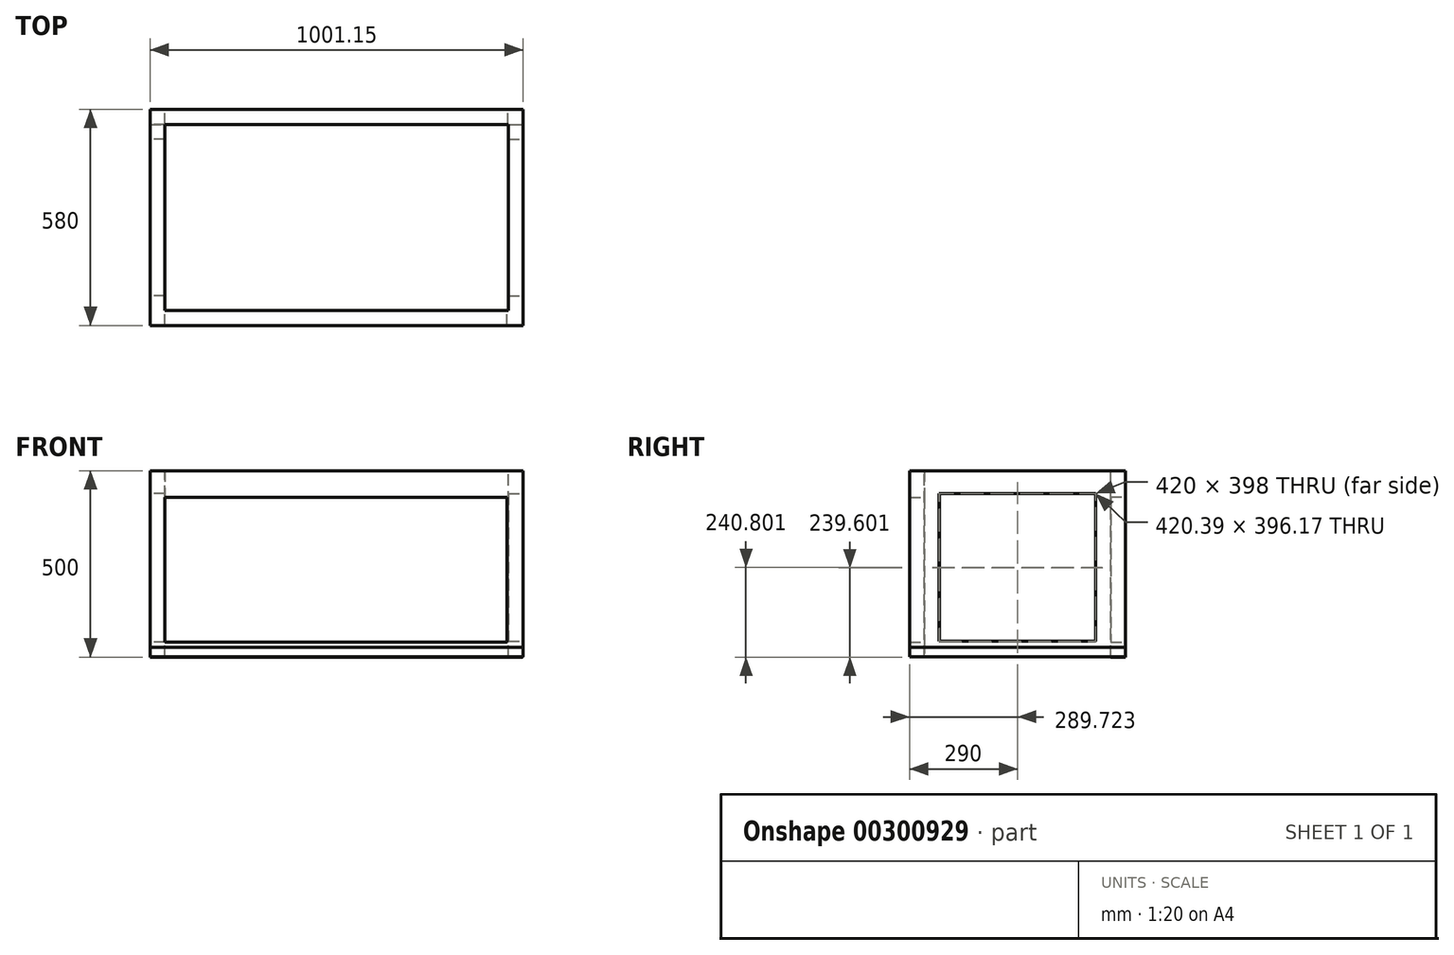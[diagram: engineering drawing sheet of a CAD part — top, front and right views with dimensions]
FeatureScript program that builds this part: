
annotation { "Feature Type Name" : "Feature", "Feature Type Description" : "" }
export const myFeature = defineFeature(function(context is Context, id is Id, definition is map)
    precondition{}
    {
        {
            var Q0;
            Q0=qCreatedBy(makeId("Front.planeOp"),FACE);
            var sketch = newSketch(context, id + "F0", { "sketchPlane" : qUnion([Q0])});
            skLineSegment(sketch, "E0.bottom", {"start": v(-500, -291.67) * mm, "end": v(500, -291.67) * mm});
            skLineSegment(sketch, "E0.top", {"start": v(-500, 208.33) * mm, "end": v(500, 208.33) * mm});
            skLineSegment(sketch, "E0.left", {"start": v(-500, -291.67) * mm, "end": v(-500, 208.33) * mm});
            skLineSegment(sketch, "E0.right", {"start": v(500, -291.67) * mm, "end": v(500, 208.33) * mm});
            skPoint(sketch, "E0.middle", {"position": v(0, -41.67) * mm});
            skLineSegment(sketch, "E1.bottom", {"start": v(-460, 138.33) * mm, "end": v(460, 138.33) * mm});
            skLineSegment(sketch, "E1.top", {"start": v(-460, -251.67) * mm, "end": v(460, -251.67) * mm});
            skLineSegment(sketch, "E1.left", {"start": v(-460, 138.33) * mm, "end": v(-460, -251.67) * mm});
            skLineSegment(sketch, "E1.right", {"start": v(460, 138.33) * mm, "end": v(460, -251.67) * mm});
            skLineSegment(sketch, "E2", {"start": v(-460, 138.33) * mm, "end": v(-500, 138.33) * mm});
            skLineSegment(sketch, "E3", {"start": v(460, 138.33) * mm, "end": v(500, 138.33) * mm});
            skSolve(sketch);
        }
        {
            var Q0;
            Q0 = qSketchRegion(id + "FjWjyGHS0iHYbx7_1", true);
            var Q1;
            {var subQ1=sQuery(id+"F0.wireOp",EDGE,"E0.top");Q1=makeQuery(id+"F0.imprint","IMPRINT",FACE,{"disambiguationData":[TD([[makeQuery(id+"F0.imprint","IMPRINT",EDGE,{"derivedFrom":subQ1}),-1.0]])]});}
            var Q2;
            {var subQ1=sQuery(id+"F0.wireOp",EDGE,"E0.bottom");Q2=makeQuery(id+"F0.imprint","IMPRINT",FACE,{"disambiguationData":[TD([[makeQuery(id+"F0.imprint","IMPRINT",EDGE,{"derivedFrom":subQ1}),1.0]])]});}
            extrude(context, id + "F1", {"entities" : qUnion([Q0, Q1, Q2]), "depth" : 40 * mm});
        }
        {
            var Q0;
            {var subQ1=sQuery(id+"F0.wireOp",EDGE,"E0.bottom");Q0=makeQuery(id+"F0.imprint","IMPRINT",FACE,{"disambiguationData":[TD([[makeQuery(id+"F0.imprint","IMPRINT",EDGE,{"derivedFrom":subQ1}),1.0]])]});}
            var Q1;
            {var subQ1=sQuery(id+"F0.wireOp",EDGE,"E0.top");Q1=makeQuery(id+"F0.imprint","IMPRINT",FACE,{"disambiguationData":[TD([[makeQuery(id+"F0.imprint","IMPRINT",EDGE,{"derivedFrom":subQ1}),-1.0]])]});}
            extrude(context, id + "F2", {"entities" : qUnion([Q0, Q1]), "depth" : 40 * mm});
        }
        {
            var Q0;
            Q0=makeQuery(id+"F2.opExtrude","SWEPT_FACE",FACE,{"disambiguationData":[OSD([sQuery(id+"F0.wireOp",EDGE,"E0.left")])]});
            var sketch = newSketch(context, id + "F3", { "sketchPlane" : qUnion([Q0])});
            skLineSegment(sketch, "E4.bottom", {"start": v(40, 146.93) * mm, "end": v(540, 146.93) * mm});
            skLineSegment(sketch, "E4.top", {"start": v(40, -291.07) * mm, "end": v(540, -291.07) * mm});
            skLineSegment(sketch, "E4.left", {"start": v(40, 146.93) * mm, "end": v(40, -291.07) * mm});
            skLineSegment(sketch, "E4.right", {"start": v(540, 146.93) * mm, "end": v(540, -291.07) * mm});
            skLineSegment(sketch, "E5.bottom", {"start": v(40, 208.33) * mm, "end": v(540, 208.33) * mm});
            skLineSegment(sketch, "E5.left", {"start": v(40, 208.33) * mm, "end": v(40, 146.93) * mm});
            skLineSegment(sketch, "E5.right", {"start": v(540, 208.33) * mm, "end": v(540, 146.93) * mm});
            skLineSegment(sketch, "E6.top", {"start": v(80, -251.07) * mm, "end": v(500, -251.07) * mm});
            skLineSegment(sketch, "E6.left", {"start": v(80, 146.93) * mm, "end": v(80, -251.07) * mm});
            skLineSegment(sketch, "E6.right", {"start": v(500, 146.93) * mm, "end": v(500, -251.07) * mm});
            skSolve(sketch);
        }
        {
            var Q0;
            Q0=makeQuery(id+"F3.imprint","IMPRINT",FACE,{"disambiguationData":[TD([[makeQuery(id+"F3.imprint","IMPRINT",EDGE,{"derivedFrom":sQuery(id+"F3.wireOp",EDGE,"E5.bottom")}),-1.0]])]});
            var Q1;
            Q1=makeQuery(id+"F3.imprint","IMPRINT",FACE,{"disambiguationData":[TD([[makeQuery(id+"F3.imprint","IMPRINT",EDGE,{"derivedFrom":sQuery(id+"F3.wireOp",EDGE,"E4.top")}),1.0]])]});
            extrude(context, id + "F4", {"entities" : qUnion([Q0, Q1]), "oppositeDirection" : true, "depth" : 40 * mm});
        }
        {
            var Q0;
            Q0=makeQuery(id+"F4.opExtrude","SWEPT_FACE",FACE,{"disambiguationData":[OSD([sQuery(id+"F3.wireOp",EDGE,"E4.right"),sQuery(id+"F3.wireOp",EDGE,"E5.right")])]});
            var sketch = newSketch(context, id + "F5", { "sketchPlane" : qUnion([Q0])});
            skLineSegment(sketch, "E7.bottom", {"start": v(-500, 208.33) * mm, "end": v(501.15, 208.33) * mm});
            skLineSegment(sketch, "E7.top", {"start": v(-500, -291.07) * mm, "end": v(501.15, -291.07) * mm});
            skLineSegment(sketch, "E7.left", {"start": v(-500, 208.33) * mm, "end": v(-500, -291.07) * mm});
            skLineSegment(sketch, "E7.right", {"start": v(501.15, 208.33) * mm, "end": v(501.15, -291.07) * mm});
            skLineSegment(sketch, "E8.bottom", {"start": v(-460, 136.56) * mm, "end": v(458.13, 136.56) * mm});
            skLineSegment(sketch, "E8.top", {"start": v(-460, -251.85) * mm, "end": v(458.13, -251.85) * mm});
            skLineSegment(sketch, "E8.left", {"start": v(-460, 136.56) * mm, "end": v(-460, -251.85) * mm});
            skLineSegment(sketch, "E8.right", {"start": v(458.13, 136.56) * mm, "end": v(458.13, -251.85) * mm});
            skSolve(sketch);
        }
        {
            var Q0;
            Q0 = qSketchRegion(id + "F5", true);
            extrude(context, id + "F6", {"entities" : qUnion([Q0]), "operationType" : NewBodyOperationType.ADD, "depth" : 40 * mm});
        }
        {
            var Q0;
            Q0=makeQuery(id+"F6.opExtrude","SWEPT_FACE",FACE,{"disambiguationData":[OSD([sQuery(id+"F5.wireOp",EDGE,"E7.right")])]});
            var sketch = newSketch(context, id + "F7", { "sketchPlane" : qUnion([Q0])});
            skLineSegment(sketch, "E9.left", {"start": v(-580, 208.33) * mm, "end": v(-580, -291.07) * mm});
            skLineSegment(sketch, "E9.right", {"start": v(0, 208.33) * mm, "end": v(0, -291.07) * mm});
            skLineSegment(sketch, "E10.bottom", {"start": v(-500.47, 147.22) * mm, "end": v(-80.08, 147.22) * mm});
            skLineSegment(sketch, "E10.top", {"start": v(-500.47, -248.95) * mm, "end": v(-80.08, -248.95) * mm});
            skLineSegment(sketch, "E10.left", {"start": v(-500.47, 147.22) * mm, "end": v(-500.47, -248.95) * mm});
            skLineSegment(sketch, "E10.right", {"start": v(-80.08, 147.22) * mm, "end": v(-80.08, -248.95) * mm});
            skLineSegment(sketch, "E11.left", {"start": v(-580, 208.33) * mm, "end": v(-580, 208.33) * mm});
            skLineSegment(sketch, "E12.bottom", {"start": v(-580, 208.33) * mm, "end": v(0, 208.33) * mm});
            skLineSegment(sketch, "E12.top", {"start": v(-580, -291.07) * mm, "end": v(0, -291.07) * mm});
            skSolve(sketch);
        }
        {
            var Q0;
            Q0 = qSketchRegion(id + "F7", true);
            extrude(context, id + "F8", {"entities" : qUnion([Q0]), "operationType" : NewBodyOperationType.ADD, "oppositeDirection" : true, "depth" : 40 * mm});
        }
        {
            var Q0;
            Q0=makeQuery(id+"F8.boolean.opBoolean","MERGE",FACE,{"derivedFrom":[makeQuery(id+"F6.boolean.opBoolean","MERGE",FACE,{"derivedFrom":[makeQuery(id+"F4.opExtrude","SWEPT_FACE",FACE,{"disambiguationData":[OSD([sQuery(id+"F3.wireOp",EDGE,"E4.top")])]}),makeQuery(id+"F6.opExtrude","SWEPT_FACE",FACE,{"disambiguationData":[OSD([sQuery(id+"F5.wireOp",EDGE,"E7.top")])]})]}),makeQuery(id+"F8.opExtrude","SWEPT_FACE",FACE,{"disambiguationData":[OSD([sQuery(id+"F7.wireOp",EDGE,"E12.top")])]})]});
            var sketch = newSketch(context, id + "F9", { "sketchPlane" : qUnion([Q0])});
            skLineSegment(sketch, "E13.bottom", {"start": v(-500, 580) * mm, "end": v(501.15, 580) * mm});
            skLineSegment(sketch, "E13.top", {"start": v(-500, 0) * mm, "end": v(501.15, 0) * mm});
            skLineSegment(sketch, "E13.left", {"start": v(-500, 580) * mm, "end": v(-500, 0) * mm});
            skLineSegment(sketch, "E13.right", {"start": v(501.15, 580) * mm, "end": v(501.15, 0) * mm});
            skSolve(sketch);
        }
        {
            var Q0;
            Q0 = qSketchRegion(id + "F9", true);
            extrude(context, id + "F10", {"entities" : qUnion([Q0]), "oppositeDirection" : true, "depth" : 25 * mm});
        }
    });
